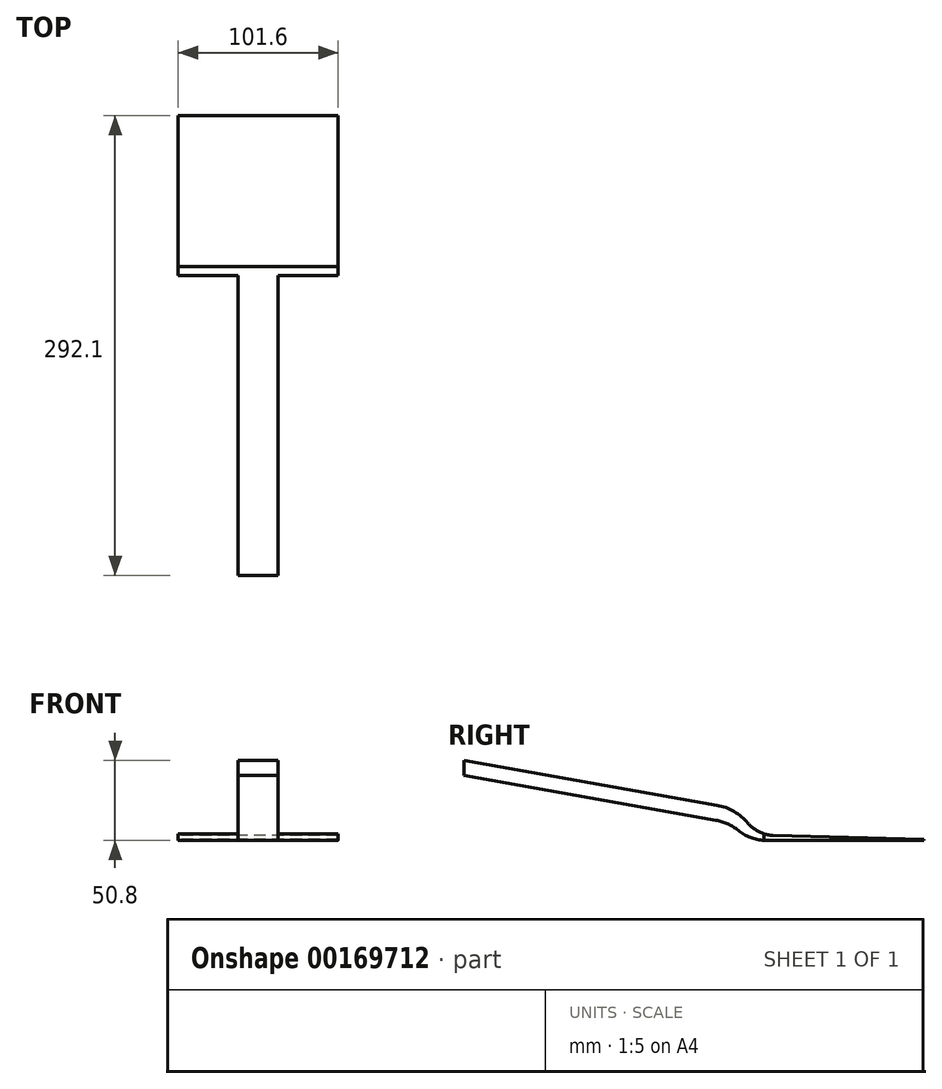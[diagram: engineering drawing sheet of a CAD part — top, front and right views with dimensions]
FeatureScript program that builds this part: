
annotation { "Feature Type Name" : "Feature", "Feature Type Description" : "" }
export const myFeature = defineFeature(function(context is Context, id is Id, definition is map)
    precondition{}
    {
        {
            var Q0;
            Q0=qCreatedBy(makeId("Top.planeOp"),FACE);
            var sketch = newSketch(context, id + "F0", { "sketchPlane" : qUnion([Q0])});
            skLineSegment(sketch, "E0.bottom", {"start": v(-50.8, 50.8) * mm, "end": v(50.8, 50.8) * mm});
            skLineSegment(sketch, "E0.top", {"start": v(-50.8, -50.8) * mm, "end": v(50.8, -50.8) * mm});
            skLineSegment(sketch, "E0.left", {"start": v(-50.8, 50.8) * mm, "end": v(-50.8, -50.8) * mm});
            skLineSegment(sketch, "E0.right", {"start": v(50.8, 50.8) * mm, "end": v(50.8, -50.8) * mm});
            skPoint(sketch, "E0.middle", {"position": v(0, 0) * mm});
            skSolve(sketch);
        }
        {
            var Q0;
            Q0=qCreatedBy(makeId("Right.planeOp"),FACE);
            var sketch = newSketch(context, id + "F1", { "sketchPlane" : qUnion([Q0])});
            skLineSegment(sketch, "E1.left", {"start": v(50.8, 0) * mm, "end": v(50.8, 0.7) * mm});
            skLineSegment(sketch, "E1.right", {"start": v(-241.3, 41.13) * mm, "end": v(-241.3, 50.8) * mm});
            skLineSegment(sketch, "E2", {"start": v(-241.3, 50.8) * mm, "end": v(-80.74, 22.3) * mm});
            skLineSegment(sketch, "E3.0", {"start": v(-241.52, 41.17) * mm, "end": v(-81.27, 12.72) * mm});
            skArc(sketch, "E4", {"start": v(-81.27, 12.72) * mm, "mid": v(-73.83, 10.4) * mm, "end": v(-67.2, 6.3) * mm});
            skLineSegment(sketch, "E5", {"start": v(50.8, 0) * mm, "end": v(-50.8, 0) * mm});
            skLineSegment(sketch, "E6", {"start": v(-50.8, 4.14) * mm, "end": v(-50.8, 0) * mm});
            skArc(sketch, "E7", {"start": v(-67.2, 6.3) * mm, "mid": v(-58.88, 1.62) * mm, "end": v(-49.47, 0) * mm});
            skArc(sketch, "E8.0", {"start": v(-80.74, 22.3) * mm, "mid": v(-69.87, 18.34) * mm, "end": v(-60.98, 10.92) * mm});
            skArc(sketch, "E9.0", {"start": v(-60.98, 10.92) * mm, "mid": v(-53.87, 5.37) * mm, "end": v(-45.14, 3.13) * mm});
            skLineSegment(sketch, "E10", {"start": v(-45.14, 3.13) * mm, "end": v(50.8, 0.7) * mm});
            skLineSegment(sketch, "E11", {"start": v(50.8, 0.7) * mm, "end": v(50.8, 0) * mm});
            skPoint(sketch, "E12.orphan", {"position": v(-50.8, 16.99) * mm});
            skSolve(sketch);
        }
        {
            var Q0;
            {var subQ3=sQuery(id+"F1.wireOp",EDGE,"E10");Q0=makeQuery(id+"F1.imprint","IMPRINT",FACE,{"disambiguationData":[TD([[makeQuery(id+"F1.imprint","IMPRINT",EDGE,{"derivedFrom":subQ3}),-1.0]])]});}
            extrude(context, id + "F2", {"entities" : qUnion([Q0]), "endBound" : BoundingType.SYMMETRIC, "depth" : 101.6 * mm});
        }
        {
            var Q0;
            {var subQ2=sQuery(id+"F1.wireOp",EDGE,"E1.right");Q0=makeQuery(id+"F1.imprint","IMPRINT",FACE,{"disambiguationData":[TD([[makeQuery(id+"F1.imprint","IMPRINT",EDGE,{"derivedFrom":subQ2}),-1.0]])]});}
            extrude(context, id + "F3", {"entities" : qUnion([Q0]), "operationType" : NewBodyOperationType.ADD, "endBound" : BoundingType.SYMMETRIC, "depth" : 25.4 * mm});
        }
    });
